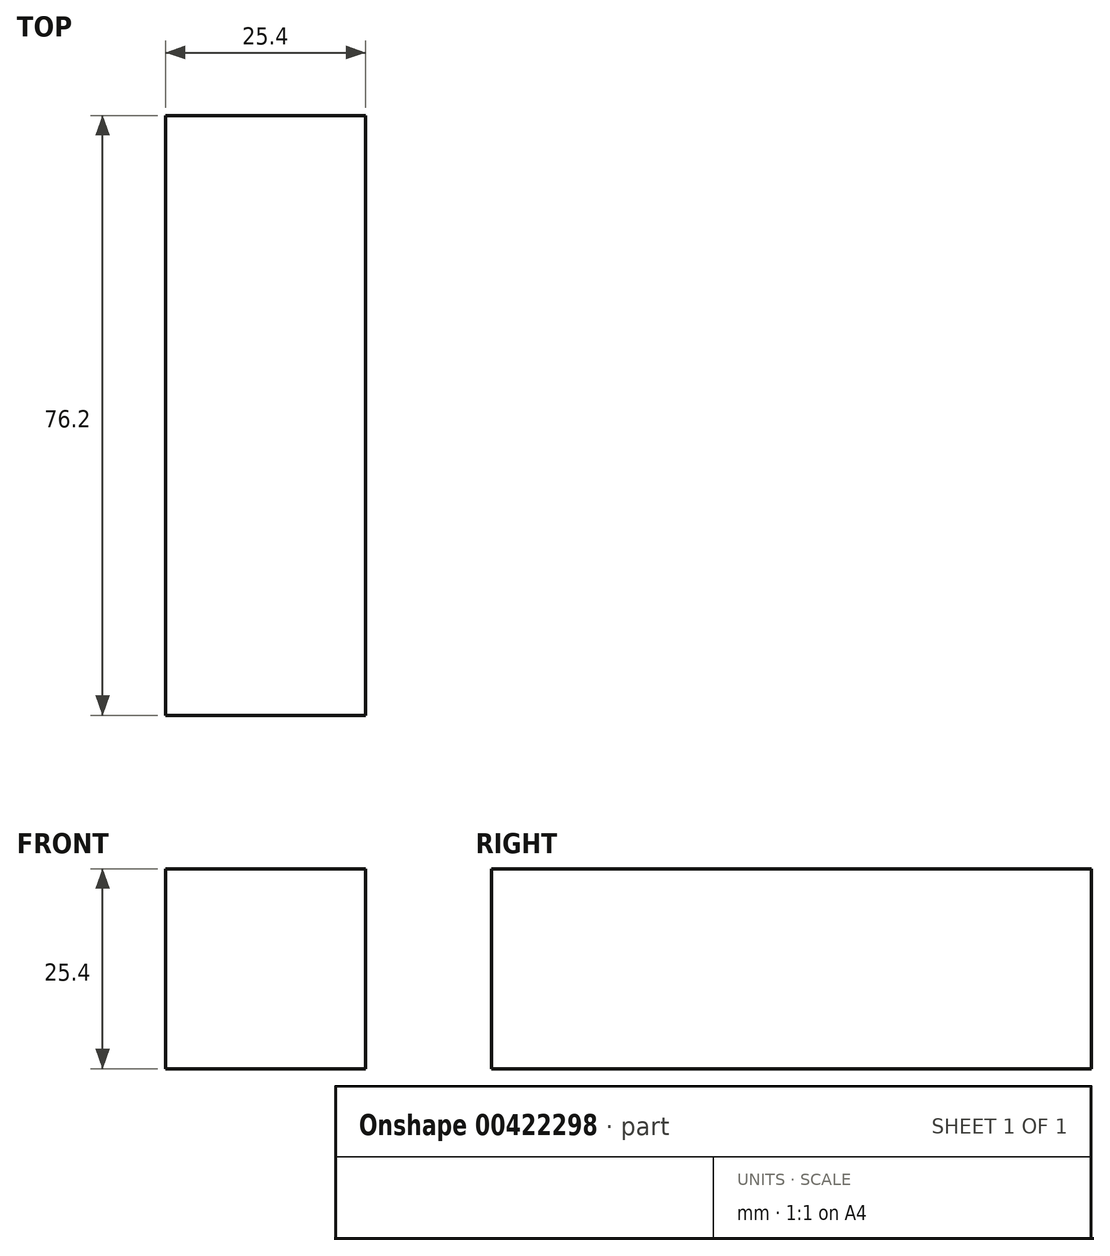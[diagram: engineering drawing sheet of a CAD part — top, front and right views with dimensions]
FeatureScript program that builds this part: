
annotation { "Feature Type Name" : "Feature", "Feature Type Description" : "" }
export const myFeature = defineFeature(function(context is Context, id is Id, definition is map)
    precondition{}
    {
        {
            var Q0;
            Q0=qCreatedBy(makeId("Front.planeOp"),FACE);
            var sketch = newSketch(context, id + "F0", { "sketchPlane" : qUnion([Q0])});
            skLineSegment(sketch, "E0.bottom", {"start": v(-28.61, 25.4) * mm, "end": v(-3.21, 25.4) * mm});
            skLineSegment(sketch, "E0.top", {"start": v(-28.61, 0) * mm, "end": v(-3.21, 0) * mm});
            skLineSegment(sketch, "E0.left", {"start": v(-28.61, 25.4) * mm, "end": v(-28.61, 0) * mm});
            skLineSegment(sketch, "E0.right", {"start": v(-3.21, 25.4) * mm, "end": v(-3.21, 0) * mm});
            skSolve(sketch);
        }
        {
            var Q0;
            Q0 = qSketchRegion(id + "F0", true);
            extrude(context, id + "F1", {"entities" : qUnion([Q0]), "depth" : 76.2 * mm});
        }
    });
